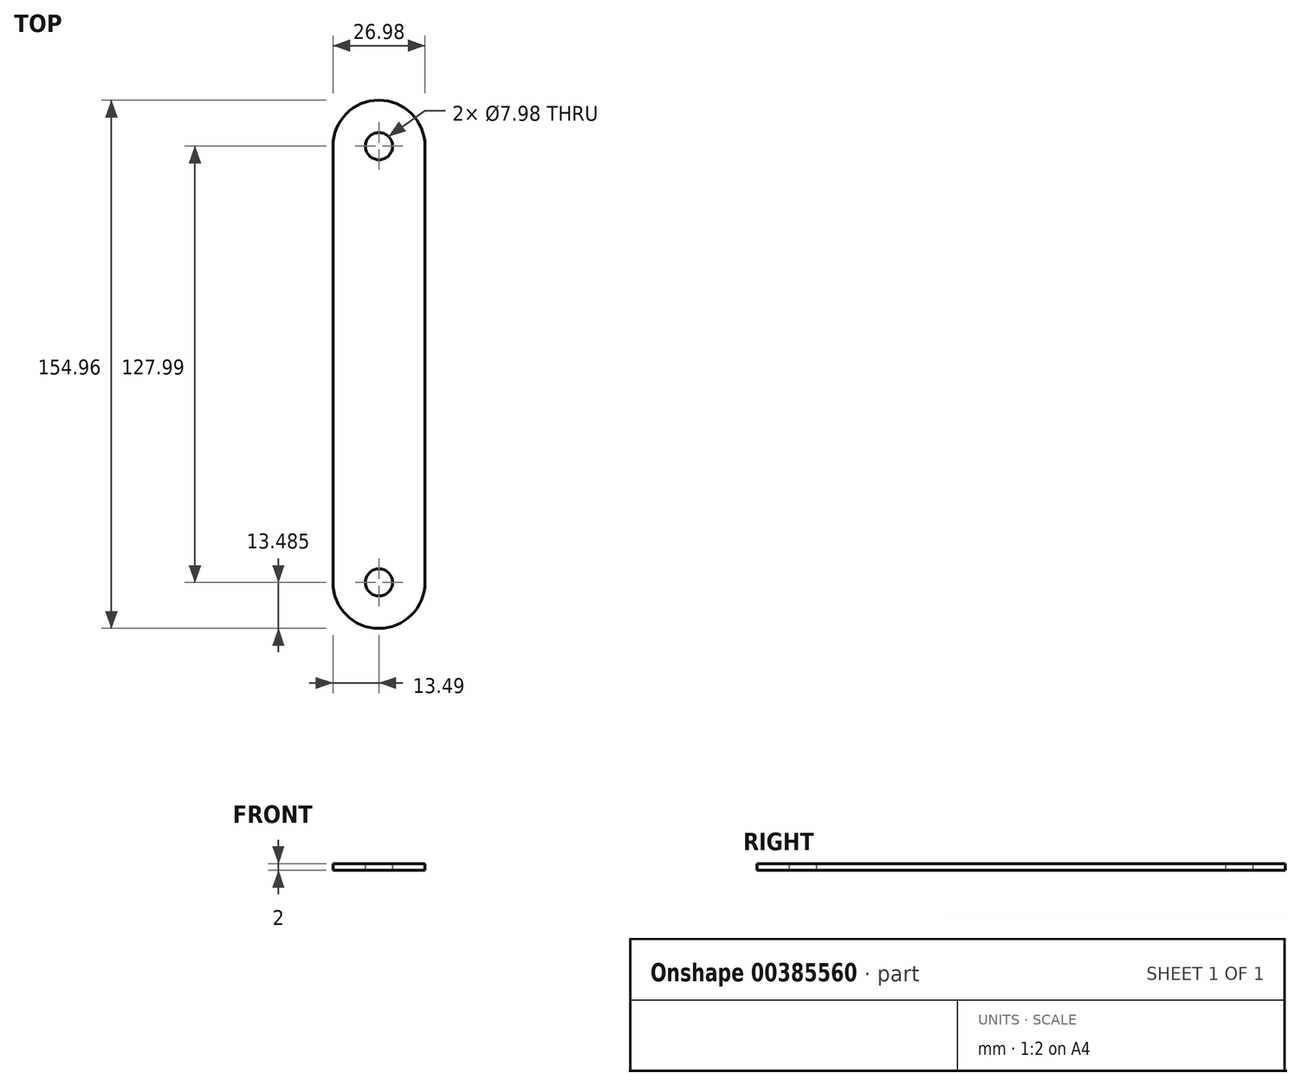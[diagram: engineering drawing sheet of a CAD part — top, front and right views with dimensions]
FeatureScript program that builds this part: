
annotation { "Feature Type Name" : "Feature", "Feature Type Description" : "" }
export const myFeature = defineFeature(function(context is Context, id is Id, definition is map)
    precondition{}
    {
        {
            var Q0;
            Q0=qCreatedBy(makeId("Top.planeOp"),FACE);
            var sketch = newSketch(context, id + "F0", { "sketchPlane" : qUnion([Q0])});
            skLineSegment(sketch, "E0.bottom", {"start": v(13.5, -77.48) * mm, "end": v(-13.49, -77.48) * mm});
            skLineSegment(sketch, "E0.top", {"start": v(13.49, 77.48) * mm, "end": v(-13.5, 77.48) * mm});
            skLineSegment(sketch, "E0.left", {"start": v(13.5, -77.48) * mm, "end": v(13.49, 77.48) * mm});
            skLineSegment(sketch, "E0.right", {"start": v(-13.49, -77.48) * mm, "end": v(-13.5, 77.48) * mm});
            skPoint(sketch, "E0.middle", {"position": v(0, 0) * mm});
            skCircle(sketch, "E1", {"center": v(0, 64) * mm, "radius": 13.5 * mm});
            skCircle(sketch, "E2", {"center": v(0, -64) * mm, "radius": 13.5 * mm});
            skCircle(sketch, "E3", {"center": v(0, 64) * mm, "radius": 4 * mm});
            skCircle(sketch, "E4", {"center": v(0, -64) * mm, "radius": 4 * mm});
            skSolve(sketch);
        }
        {
            var Q0;
            Q0 = qSketchRegion(id + "F0", true);
            extrude(context, id + "F1", {"entities" : qUnion([Q0]), "depth" : 2 * mm});
        }
        {
            var Q0;
            {var subQ0=sQuery(id+"F0.wireOp",EDGE,"E0.left");var subQ1=sQuery(id+"F0.wireOp",EDGE,"E0.top");var subQ2=makeQuery(id+"F0.imprint","INTERSECT",VERTEX,{"derivedFrom":[subQ1,subQ0]});Q0=makeQuery(id+"F0.imprint","IMPRINT",FACE,{"disambiguationData":[TD([[makeQuery(id+"F0.imprint","IMPRINT",EDGE,{"disambiguationData":[TD([[subQ2,-1.0]])],"derivedFrom":subQ1}),1.0]])]});}
            var Q1;
            {var subQ0=sQuery(id+"F0.wireOp",EDGE,"E0.right");var subQ1=sQuery(id+"F0.wireOp",EDGE,"E0.top");var subQ2=makeQuery(id+"F0.imprint","INTERSECT",VERTEX,{"derivedFrom":[subQ1,subQ0]});Q1=makeQuery(id+"F0.imprint","IMPRINT",FACE,{"disambiguationData":[TD([[makeQuery(id+"F0.imprint","IMPRINT",EDGE,{"disambiguationData":[TD([[subQ2,1.0]])],"derivedFrom":subQ1}),1.0]])]});}
            var Q2;
            {var subQ0=sQuery(id+"F0.wireOp",EDGE,"E0.left");var subQ1=sQuery(id+"F0.wireOp",EDGE,"E0.bottom");var subQ2=makeQuery(id+"F0.imprint","INTERSECT",VERTEX,{"derivedFrom":[subQ1,subQ0]});Q2=makeQuery(id+"F0.imprint","IMPRINT",FACE,{"disambiguationData":[TD([[makeQuery(id+"F0.imprint","IMPRINT",EDGE,{"disambiguationData":[TD([[subQ2,-1.0]])],"derivedFrom":subQ1}),-1.0]])]});}
            var Q3;
            {var subQ0=sQuery(id+"F0.wireOp",EDGE,"E0.right");var subQ1=sQuery(id+"F0.wireOp",EDGE,"E0.bottom");var subQ2=makeQuery(id+"F0.imprint","INTERSECT",VERTEX,{"derivedFrom":[subQ1,subQ0]});Q3=makeQuery(id+"F0.imprint","IMPRINT",FACE,{"disambiguationData":[TD([[makeQuery(id+"F0.imprint","IMPRINT",EDGE,{"disambiguationData":[TD([[subQ2,1.0]])],"derivedFrom":subQ1}),-1.0]])]});}
            extrude(context, id + "F2", {"entities" : qUnion([Q0, Q1, Q2, Q3]), "operationType" : NewBodyOperationType.REMOVE, "depth" : 25 * mm});
        }
    });
